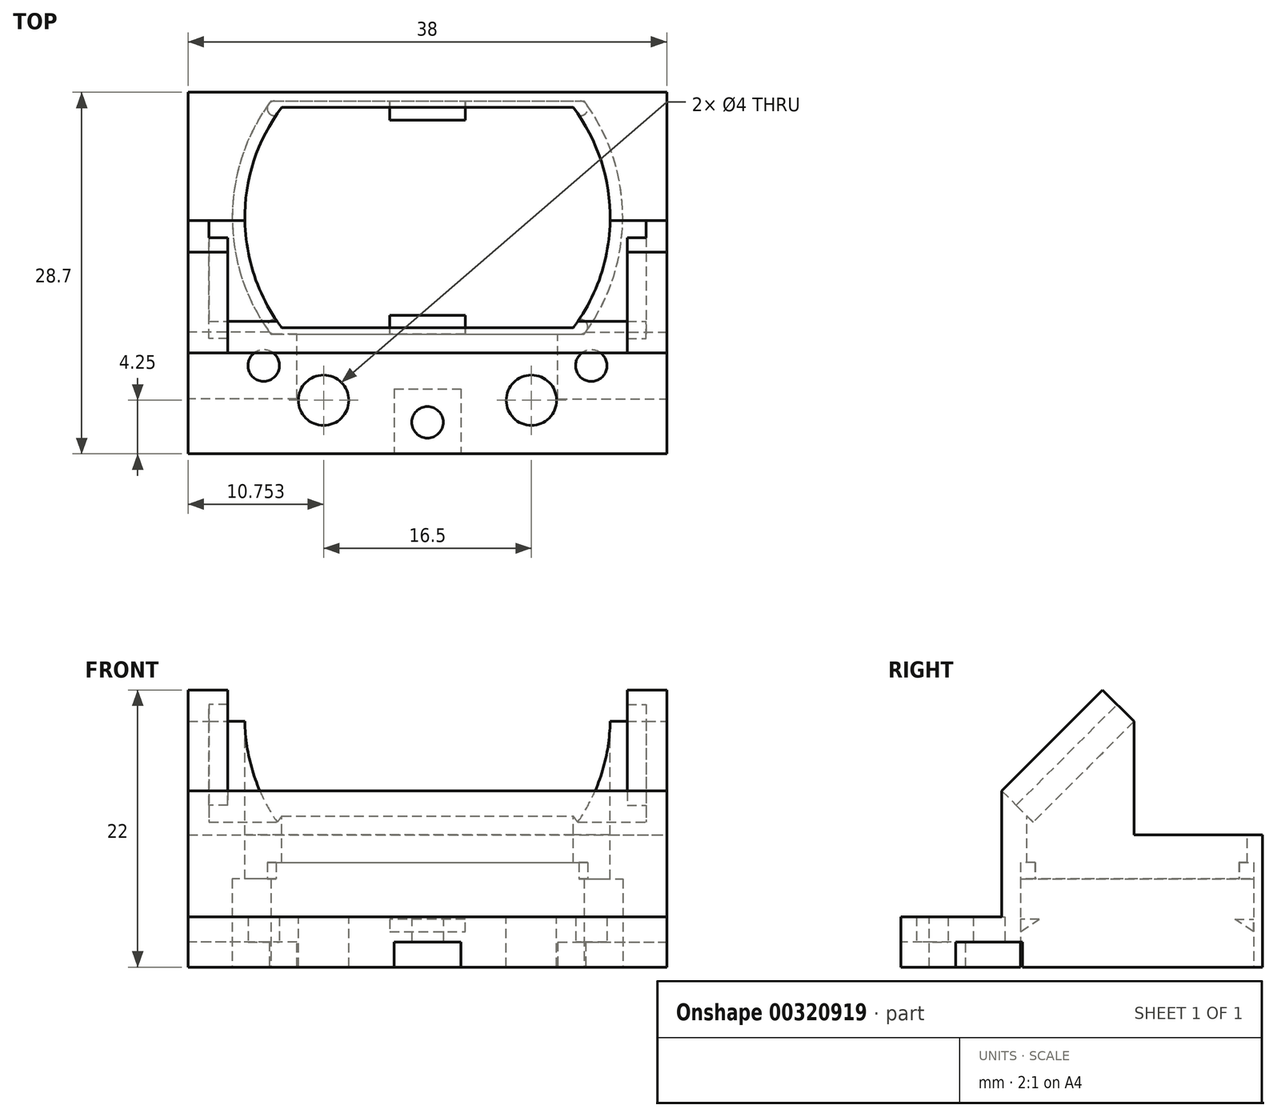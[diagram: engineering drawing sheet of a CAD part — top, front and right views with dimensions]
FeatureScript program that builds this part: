
annotation { "Feature Type Name" : "Feature", "Feature Type Description" : "" }
export const myFeature = defineFeature(function(context is Context, id is Id, definition is map)
    precondition{}
    {
        {
            var Q0;
            Q0=qCreatedBy(makeId("Top.planeOp"),FACE);
            var sketch = newSketch(context, id + "F0", { "sketchPlane" : qUnion([Q0])});
            skLineSegment(sketch, "E0.bottom", {"start": v(-15.89, 0) * mm, "end": v(22.11, 0) * mm});
            skLineSegment(sketch, "E0.top", {"start": v(-15.89, 28.5) * mm, "end": v(22.11, 28.5) * mm});
            skLineSegment(sketch, "E0.left", {"start": v(-15.89, 0) * mm, "end": v(-15.89, 28.5) * mm});
            skLineSegment(sketch, "E0.right", {"start": v(22.11, 0) * mm, "end": v(22.11, 28.5) * mm});
            skSolve(sketch);
        }
        {
            var Q0;
            Q0=qSketchRegion(id+"F0",true);
            extrude(context, id + "F1", {"entities" : qUnion([Q0]), "depth" : 19.5 * mm});
        }
        {
            var Q0;
            Q0=makeQuery(id+"F1.opExtrude","SWEPT_FACE",FACE,{"disambiguationData":[OSD([sQuery(id+"F0.wireOp",EDGE,"E0.right")])]});
            var sketch = newSketch(context, id + "F2", { "sketchPlane" : qUnion([Q0])});
            skLineSegment(sketch, "E1.bottom", {"start": v(0, 19.5) * mm, "end": v(8, 19.5) * mm});
            skLineSegment(sketch, "E1.top", {"start": v(0, 4) * mm, "end": v(8, 4) * mm});
            skLineSegment(sketch, "E1.left", {"start": v(0, 19.5) * mm, "end": v(0, 4) * mm});
            skLineSegment(sketch, "E1.right", {"start": v(8, 19.5) * mm, "end": v(8, 4) * mm});
            skSolve(sketch);
        }
        {
            var Q0;
            {var subQ4=sQuery(id+"F2.wireOp",EDGE,"E1.top");Q0=makeQuery(id+"F2.imprint","IMPRINT",FACE,{"disambiguationData":[TD([[makeQuery(id+"F2.imprint","IMPRINT",EDGE,{"derivedFrom":subQ4}),-1.0]])]});}
            var sketch = newSketch(context, id + "F3", { "sketchPlane" : qUnion([Q0])});
            skLineSegment(sketch, "E2.bottom", {"start": v(28.5, 19.5) * mm, "end": v(18.5, 19.5) * mm});
            skLineSegment(sketch, "E2.top", {"start": v(28.5, 10.5) * mm, "end": v(18.5, 10.5) * mm});
            skLineSegment(sketch, "E2.left", {"start": v(28.5, 19.5) * mm, "end": v(28.5, 10.5) * mm});
            skLineSegment(sketch, "E2.right", {"start": v(18.5, 19.5) * mm, "end": v(18.5, 10.5) * mm});
            skSolve(sketch);
        }
        {
            var Q0;
            Q0=makeQuery(id+"F2.imprint","IMPRINT",FACE,{"disambiguationData":[TD([[makeQuery(id+"F2.imprint","IMPRINT",EDGE,{"derivedFrom":sQuery(id+"F2.wireOp",EDGE,"E1.bottom")}),-1.0]])]});
            extrude(context, id + "F4", {"entities" : qUnion([Q0]), "operationType" : NewBodyOperationType.REMOVE, "oppositeDirection" : true, "depth" : 38 * mm});
        }
        {
            var Q0;
            Q0=makeQuery(id+"F1.opExtrude","CAP_FACE",FACE,{"disambiguationData":[OSD([sQuery(id+"F0.wireOp",EDGE,"E0.bottom"),sQuery(id+"F0.wireOp",EDGE,"E0.top"),sQuery(id+"F0.wireOp",EDGE,"E0.left"),sQuery(id+"F0.wireOp",EDGE,"E0.right")])],"isStart":false});
            var sketch = newSketch(context, id + "F5", { "sketchPlane" : qUnion([Q0])});
            skLineSegment(sketch, "E3.bottom", {"start": v(-8.45, 10) * mm, "end": v(14.68, 10) * mm});
            skLineSegment(sketch, "E3.top", {"start": v(-8.45, 27.5) * mm, "end": v(14.68, 27.5) * mm});
            skArc(sketch, "E4", {"start": v(14.68, 10) * mm, "mid": v(17.61, 18.75) * mm, "end": v(14.68, 27.5) * mm});
            skArc(sketch, "E5.trimOffspring", {"start": v(-8.45, 27.5) * mm, "mid": v(-11.39, 18.75) * mm, "end": v(-8.45, 10) * mm});
            skSolve(sketch);
        }
        {
            var Q0;
            Q0=qSketchRegion(id+"F5",true);
            extrude(context, id + "F6", {"entities" : qUnion([Q0]), "operationType" : NewBodyOperationType.REMOVE, "oppositeDirection" : true, "depth" : 19.5 * mm});
        }
        {
            var Q0;
            Q0=makeQuery(id+"F3.imprint","IMPRINT",FACE,{"disambiguationData":[TD([[makeQuery(id+"F3.imprint","IMPRINT",EDGE,{"derivedFrom":sQuery(id+"F3.wireOp",EDGE,"E2.bottom")}),-1.0]])]});
            extrude(context, id + "F7", {"entities" : qUnion([Q0]), "operationType" : NewBodyOperationType.REMOVE, "oppositeDirection" : true, "depth" : 38 * mm});
        }
        {
            var Q0;
            Q0=makeQuery(id+"F1.opExtrude","SWEPT_FACE",FACE,{"disambiguationData":[OSD([sQuery(id+"F0.wireOp",EDGE,"E0.right")])]});
            var sketch = newSketch(context, id + "F8", { "sketchPlane" : qUnion([Q0])});
            skLineSegment(sketch, "E6.bottom", {"start": v(8, 19.5) * mm, "end": v(18.5, 19.5) * mm});
            skLineSegment(sketch, "E6.left", {"start": v(8, 19.5) * mm, "end": v(8, 14) * mm});
            skLineSegment(sketch, "E7", {"start": v(18.5, 19.5) * mm, "end": v(10.5, 11.5) * mm});
            skLineSegment(sketch, "E8", {"start": v(8, 14) * mm, "end": v(10.5, 11.5) * mm});
            skSolve(sketch);
        }
        {
            var Q0;
            Q0=qSketchRegion(id+"F8",true);
            extrude(context, id + "F9", {"entities" : qUnion([Q0]), "operationType" : NewBodyOperationType.REMOVE, "oppositeDirection" : true, "depth" : 38 * mm});
        }
        {
            var Q0;
            Q0=makeQuery(id+"F1.opExtrude","CAP_FACE",FACE,{"disambiguationData":[OSD([sQuery(id+"F0.wireOp",EDGE,"E0.bottom"),sQuery(id+"F0.wireOp",EDGE,"E0.top"),sQuery(id+"F0.wireOp",EDGE,"E0.left"),sQuery(id+"F0.wireOp",EDGE,"E0.right")])],"isStart":true});
            var sketch = newSketch(context, id + "F10", { "sketchPlane" : qUnion([Q0])});
            skLineSegment(sketch, "E9.bottom", {"start": v(-9.32, -9.5) * mm, "end": v(15.55, -9.5) * mm});
            skLineSegment(sketch, "E9.top", {"start": v(-9.32, -28) * mm, "end": v(15.55, -28) * mm});
            skArc(sketch, "E10", {"start": v(-9.32, -9.5) * mm, "mid": v(-12.39, -18.75) * mm, "end": v(-9.32, -28) * mm});
            skArc(sketch, "E11.trimOffspring", {"start": v(15.55, -28) * mm, "mid": v(18.61, -18.75) * mm, "end": v(15.55, -9.5) * mm});
            skSolve(sketch);
        }
        {
            var Q0;
            Q0=qSketchRegion(id+"F10",true);
            extrude(context, id + "F11", {"entities" : qUnion([Q0]), "operationType" : NewBodyOperationType.REMOVE, "oppositeDirection" : true, "depth" : 7 * mm});
        }
        {
            var Q0;
            Q0=makeQuery(id+"F4.boolean.opBoolean","COPY",FACE,{"derivedFrom":makeQuery(id+"F4.opExtrude","SWEPT_FACE",FACE,{"disambiguationData":[OSD([sQuery(id+"F2.wireOp",EDGE,"E1.top")])]})});
            var sketch = newSketch(context, id + "F12", { "sketchPlane" : qUnion([Q0])});
            skCircle(sketch, "E12", {"center": v(-5.14, 4.25) * mm, "radius": 2 * mm});
            skCircle(sketch, "E13", {"center": v(11.36, 4.25) * mm, "radius": 2 * mm});
            skSolve(sketch);
        }
        {
            var Q0;
            Q0=makeQuery(id+"F12.imprint","IMPRINT",FACE,{"disambiguationData":[TD([[makeQuery(id+"F12.imprint","IMPRINT",EDGE,{"derivedFrom":sQuery(id+"F12.wireOp",EDGE,"E12")}),1.0]])]});
            var Q1;
            Q1=makeQuery(id+"F12.imprint","IMPRINT",FACE,{"disambiguationData":[TD([[makeQuery(id+"F12.imprint","IMPRINT",EDGE,{"derivedFrom":sQuery(id+"F12.wireOp",EDGE,"E13")}),1.0]])]});
            extrude(context, id + "F13", {"entities" : qUnion([Q0, Q1]), "operationType" : NewBodyOperationType.REMOVE, "oppositeDirection" : true, "depth" : 4 * mm});
        }
        {
            var Q0;
            Q0=makeQuery(id+"F1.opExtrude","SWEPT_FACE",FACE,{"disambiguationData":[OSD([sQuery(id+"F0.wireOp",EDGE,"E0.right")])]});
            var sketch = newSketch(context, id + "F14", { "sketchPlane" : qUnion([Q0])});
            skLineSegment(sketch, "E14", {"start": v(10.5, 11.5) * mm, "end": v(18.5, 19.5) * mm});
            skLineSegment(sketch, "E15", {"start": v(10.5, 11.5) * mm, "end": v(8, 14) * mm});
            skLineSegment(sketch, "E16", {"start": v(8, 14) * mm, "end": v(16, 22) * mm});
            skLineSegment(sketch, "E17", {"start": v(16, 22) * mm, "end": v(18.5, 19.5) * mm});
            skSolve(sketch);
        }
        {
            var Q0;
            Q0 = qSketchRegion(id + "F14", true);
            extrude(context, id + "F15", {"entities" : qUnion([Q0]), "operationType" : NewBodyOperationType.ADD, "oppositeDirection" : true, "depth" : 1.65 * mm, "offsetDistance" : 25 * mm});
        }
        {
            var Q0;
            Q0=makeQuery(id+"F15.opExtrude","CAP_FACE",FACE,{"disambiguationData":[OSD([sQuery(id+"F14.wireOp",EDGE,"E14"),sQuery(id+"F14.wireOp",EDGE,"E15"),sQuery(id+"F14.wireOp",EDGE,"E16"),sQuery(id+"F14.wireOp",EDGE,"E17")])],"isStart":false});
            var sketch = newSketch(context, id + "F16", { "sketchPlane" : qUnion([Q0])});
            skLineSegment(sketch, "E18", {"start": v(-8, 14) * mm, "end": v(-16, 22) * mm});
            skLineSegment(sketch, "E19", {"start": v(-16, 22) * mm, "end": v(-17.16, 20.84) * mm});
            skLineSegment(sketch, "E20", {"start": v(-17.16, 20.84) * mm, "end": v(-9.16, 12.84) * mm});
            skLineSegment(sketch, "E21", {"start": v(-9.16, 12.84) * mm, "end": v(-8, 14) * mm});
            skSolve(sketch);
        }
        {
            var Q0;
            Q0=makeQuery(id+"F16.imprint","IMPRINT",FACE,{"disambiguationData":[TD([[makeQuery(id+"F16.imprint","IMPRINT",EDGE,{"derivedFrom":sQuery(id+"F16.wireOp",EDGE,"E18")}),1.0]])]});
            extrude(context, id + "F17", {"entities" : qUnion([Q0]), "operationType" : NewBodyOperationType.ADD, "depth" : 1.5 * mm});
        }
        {
            var Q0;
            Q0=makeQuery(id+"F1.opExtrude","SWEPT_FACE",FACE,{"disambiguationData":[OSD([sQuery(id+"F0.wireOp",EDGE,"E0.left")])]});
            var sketch = newSketch(context, id + "F18", { "sketchPlane" : qUnion([Q0])});
            skLineSegment(sketch, "E22", {"start": v(-10.5, 11.5) * mm, "end": v(-8, 14) * mm});
            skLineSegment(sketch, "E23", {"start": v(-8, 14) * mm, "end": v(-16, 22) * mm});
            skLineSegment(sketch, "E24", {"start": v(-16, 22) * mm, "end": v(-18.5, 19.5) * mm});
            skLineSegment(sketch, "E25", {"start": v(-18.5, 19.5) * mm, "end": v(-10.5, 11.5) * mm});
            skSolve(sketch);
        }
        {
            var Q0;
            Q0=makeQuery(id+"F18.imprint","IMPRINT",FACE,{"disambiguationData":[TD([[makeQuery(id+"F18.imprint","IMPRINT",EDGE,{"derivedFrom":sQuery(id+"F18.wireOp",EDGE,"E22")}),-1.0]])]});
            extrude(context, id + "F19", {"entities" : qUnion([Q0]), "operationType" : NewBodyOperationType.ADD, "oppositeDirection" : true, "depth" : 1.65 * mm, "offsetDistance" : 25 * mm});
        }
        {
            var Q0;
            Q0=makeQuery(id+"F19.opExtrude","CAP_FACE",FACE,{"disambiguationData":[OSD([sQuery(id+"F18.wireOp",EDGE,"E22"),sQuery(id+"F18.wireOp",EDGE,"E23"),sQuery(id+"F18.wireOp",EDGE,"E24"),sQuery(id+"F18.wireOp",EDGE,"E25")])],"isStart":false});
            var sketch = newSketch(context, id + "F20", { "sketchPlane" : qUnion([Q0])});
            skLineSegment(sketch, "E26", {"start": v(16, 22) * mm, "end": v(8, 14) * mm});
            skLineSegment(sketch, "E27", {"start": v(8, 14) * mm, "end": v(9.16, 12.84) * mm});
            skLineSegment(sketch, "E28", {"start": v(9.16, 12.84) * mm, "end": v(17.16, 20.84) * mm});
            skLineSegment(sketch, "E29", {"start": v(17.16, 20.84) * mm, "end": v(16, 22) * mm});
            skSolve(sketch);
        }
        {
            var Q0;
            Q0 = qSketchRegion(id + "F20", true);
            extrude(context, id + "F21", {"entities" : qUnion([Q0]), "operationType" : NewBodyOperationType.ADD, "depth" : 1.5 * mm});
        }
        {
            var Q0;
            Q0=makeQuery(id+"F11.boolean.opBoolean","COPY",FACE,{"derivedFrom":makeQuery(id+"F11.opExtrude","SWEPT_FACE",FACE,{"disambiguationData":[OSD([sQuery(id+"F10.wireOp",EDGE,"E9.bottom")])]})});
            var sketch = newSketch(context, id + "F22", { "sketchPlane" : qUnion([Q0])});
            skLineSegment(sketch, "E30", {"start": v(-3.11, 3.8) * mm, "end": v(-0.11, 3.8) * mm});
            skPoint(sketch, "E30.startSnap0", {"position": v(-3.11, 7) * mm});
            skLineSegment(sketch, "E31", {"start": v(-0.11, 3.8) * mm, "end": v(-0.11, 2.8) * mm});
            skLineSegment(sketch, "E32", {"start": v(-0.11, 2.8) * mm, "end": v(-6.11, 2.8) * mm});
            skLineSegment(sketch, "E33", {"start": v(-6.11, 2.8) * mm, "end": v(-6.11, 3.8) * mm});
            skLineSegment(sketch, "E34", {"start": v(-6.11, 3.8) * mm, "end": v(-3.11, 3.8) * mm});
            skSolve(sketch);
        }
        {
            var Q0;
            Q0 = qSketchRegion(id + "F22", true);
            extrude(context, id + "F23", {"entities" : qUnion([Q0]), "operationType" : NewBodyOperationType.ADD, "depth" : 1.5 * mm});
        }
        {
            var Q0;
            Q0=makeQuery(id+"F23.opExtrude","SWEPT_FACE",FACE,{"disambiguationData":[OSD([sQuery(id+"F22.wireOp",EDGE,"E31")])]});
            var sketch = newSketch(context, id + "F24", { "sketchPlane" : qUnion([Q0])});
            skLineSegment(sketch, "E35", {"start": v(-9.5, 2.8) * mm, "end": v(-11, 3.8) * mm});
            skLineSegment(sketch, "E36", {"start": v(-11, 3.8) * mm, "end": v(-11, 2.8) * mm});
            skLineSegment(sketch, "E37", {"start": v(-11, 2.8) * mm, "end": v(-9.5, 2.8) * mm});
            skSolve(sketch);
        }
        {
            var Q0;
            Q0 = qSketchRegion(id + "F24", true);
            extrude(context, id + "F25", {"entities" : qUnion([Q0]), "operationType" : NewBodyOperationType.REMOVE, "oppositeDirection" : true, "depth" : 6 * mm});
        }
        {
            var Q0;
            Q0=makeQuery(id+"F11.boolean.opBoolean","COPY",FACE,{"derivedFrom":makeQuery(id+"F11.opExtrude","SWEPT_FACE",FACE,{"disambiguationData":[OSD([sQuery(id+"F10.wireOp",EDGE,"E9.top")])]})});
            var sketch = newSketch(context, id + "F26", { "sketchPlane" : qUnion([Q0])});
            skLineSegment(sketch, "E38", {"start": v(3.11, 3.8) * mm, "end": v(6.11, 3.8) * mm});
            skPoint(sketch, "E38.startSnap0", {"position": v(3.11, 7) * mm});
            skLineSegment(sketch, "E39", {"start": v(6.11, 3.8) * mm, "end": v(6.11, 2.8) * mm});
            skLineSegment(sketch, "E40", {"start": v(6.11, 2.8) * mm, "end": v(0.11, 2.8) * mm});
            skLineSegment(sketch, "E41", {"start": v(0.11, 2.8) * mm, "end": v(0.11, 3.8) * mm});
            skLineSegment(sketch, "E42", {"start": v(0.11, 3.8) * mm, "end": v(3.11, 3.8) * mm});
            skSolve(sketch);
        }
        {
            var Q0;
            Q0 = qSketchRegion(id + "F26", true);
            extrude(context, id + "F27", {"entities" : qUnion([Q0]), "operationType" : NewBodyOperationType.ADD, "depth" : 1.5 * mm});
        }
        {
            var Q0;
            Q0=makeQuery(id+"F27.opExtrude","SWEPT_FACE",FACE,{"disambiguationData":[OSD([sQuery(id+"F26.wireOp",EDGE,"E41")])]});
            var sketch = newSketch(context, id + "F28", { "sketchPlane" : qUnion([Q0])});
            skLineSegment(sketch, "E43", {"start": v(-28, 2.8) * mm, "end": v(-26.5, 3.8) * mm});
            skLineSegment(sketch, "E44", {"start": v(-26.5, 3.8) * mm, "end": v(-26.5, 2.8) * mm});
            skLineSegment(sketch, "E45", {"start": v(-26.5, 2.8) * mm, "end": v(-28, 2.8) * mm});
            skSolve(sketch);
        }
        {
            var Q0;
            Q0 = qSketchRegion(id + "F28", true);
            extrude(context, id + "F29", {"entities" : qUnion([Q0]), "operationType" : NewBodyOperationType.REMOVE, "oppositeDirection" : true, "depth" : 6 * mm});
        }
        {
            var Q0;
            Q0=makeQuery(id+"F1.opExtrude","SWEPT_FACE",FACE,{"disambiguationData":[OSD([sQuery(id+"F0.wireOp",EDGE,"E0.top")])]});
            var sketch = newSketch(context, id + "F30", { "sketchPlane" : qUnion([Q0])});
            skLineSegment(sketch, "E46.bottom", {"start": v(15.89, 0) * mm, "end": v(-22.11, 0) * mm});
            skLineSegment(sketch, "E46.top", {"start": v(15.89, 10.5) * mm, "end": v(-22.11, 10.5) * mm});
            skLineSegment(sketch, "E46.left", {"start": v(15.89, 0) * mm, "end": v(15.89, 10.5) * mm});
            skLineSegment(sketch, "E46.right", {"start": v(-22.11, 0) * mm, "end": v(-22.11, 10.5) * mm});
            skSolve(sketch);
        }
        {
            var Q0;
            Q0 = qSketchRegion(id + "F30", true);
            extrude(context, id + "F31", {"entities" : qUnion([Q0]), "operationType" : NewBodyOperationType.ADD, "depth" : 0.2 * mm});
        }
        {
            var Q0;
            Q0=makeQuery(id+"F11.boolean.opBoolean","COPY",FACE,{"derivedFrom":makeQuery(id+"F11.opExtrude","CAP_FACE",FACE,{"disambiguationData":[OSD([sQuery(id+"F10.wireOp",EDGE,"E9.bottom"),sQuery(id+"F10.wireOp",EDGE,"E9.top"),sQuery(id+"F10.wireOp",EDGE,"E10"),sQuery(id+"F10.wireOp",EDGE,"E11.trimOffspring")])],"isStart":false})});
            var sketch = newSketch(context, id + "F32", { "sketchPlane" : qUnion([Q0])});
            skLineSegment(sketch, "E47", {"start": v(-8.45, -10.08) * mm, "end": v(-8.45, -27.42) * mm});
            skLineSegment(sketch, "E48", {"start": v(-9.03, -28) * mm, "end": v(15.26, -28) * mm});
            skLineSegment(sketch, "E49", {"start": v(14.68, -27.42) * mm, "end": v(14.68, -10.08) * mm});
            skLineSegment(sketch, "E50", {"start": v(15.26, -9.5) * mm, "end": v(-9.03, -9.5) * mm});
            skArc(sketch, "E51", {"start": v(-8.45, -27.42) * mm, "mid": v(-9.44, -27) * mm, "end": v(-9.03, -28) * mm});
            skArc(sketch, "E52", {"start": v(-9.03, -9.5) * mm, "mid": v(-9.44, -10.5) * mm, "end": v(-8.45, -10.08) * mm});
            skPoint(sketch, "E53.orphan", {"position": v(-8.45, -9.5) * mm});
            skArc(sketch, "E54", {"start": v(15.26, -28) * mm, "mid": v(15.67, -27) * mm, "end": v(14.68, -27.42) * mm});
            skPoint(sketch, "E55.orphan", {"position": v(14.68, -28) * mm});
            skArc(sketch, "E56", {"start": v(14.68, -10.08) * mm, "mid": v(15.67, -10.5) * mm, "end": v(15.26, -9.5) * mm});
            skSolve(sketch);
        }
        {
            var Q0;
            Q0 = qSketchRegion(id + "F32", true);
            extrude(context, id + "F33", {"entities" : qUnion([Q0]), "operationType" : NewBodyOperationType.REMOVE, "oppositeDirection" : true, "depth" : 1.3 * mm});
        }
        {
            var Q0;
            Q0=makeQuery(id+"F31.boolean.opBoolean","MERGE",FACE,{"derivedFrom":[makeQuery(id+"F1.opExtrude","CAP_FACE",FACE,{"disambiguationData":[OSD([sQuery(id+"F0.wireOp",EDGE,"E0.bottom"),sQuery(id+"F0.wireOp",EDGE,"E0.top"),sQuery(id+"F0.wireOp",EDGE,"E0.left"),sQuery(id+"F0.wireOp",EDGE,"E0.right")])],"isStart":true}),makeQuery(id+"F31.opExtrude","SWEPT_FACE",FACE,{"disambiguationData":[OSD([sQuery(id+"F30.wireOp",EDGE,"E46.bottom")])]})]});
            var sketch = newSketch(context, id + "F34", { "sketchPlane" : qUnion([Q0])});
            skCircle(sketch, "E57", {"center": v(-9.89, -7) * mm, "radius": 1.25 * mm});
            skCircle(sketch, "E58", {"center": v(16.11, -7) * mm, "radius": 1.25 * mm});
            skCircle(sketch, "E59", {"center": v(3.11, -2.5) * mm, "radius": 1.25 * mm});
            skSolve(sketch);
        }
        {
            var Q0;
            Q0 = qSketchRegion(id + "F34", true);
            extrude(context, id + "F35", {"entities" : qUnion([Q0]), "operationType" : NewBodyOperationType.REMOVE, "oppositeDirection" : true, "depth" : 4 * mm, "offsetDistance" : 25 * mm});
        }
        {
            var Q0;
            Q0=makeQuery(id+"F31.boolean.opBoolean","MERGE",FACE,{"derivedFrom":[makeQuery(id+"F19.boolean.opBoolean","MERGE",FACE,{"derivedFrom":[makeQuery(id+"F1.opExtrude","SWEPT_FACE",FACE,{"disambiguationData":[OSD([sQuery(id+"F0.wireOp",EDGE,"E0.left")])]}),makeQuery(id+"F19.opExtrude","CAP_FACE",FACE,{"disambiguationData":[OSD([sQuery(id+"F18.wireOp",EDGE,"E22"),sQuery(id+"F18.wireOp",EDGE,"E23"),sQuery(id+"F18.wireOp",EDGE,"E24"),sQuery(id+"F18.wireOp",EDGE,"E25")])],"isStart":true})]}),makeQuery(id+"F31.opExtrude","SWEPT_FACE",FACE,{"disambiguationData":[OSD([sQuery(id+"F30.wireOp",EDGE,"E46.left")])]})]});
            var sketch = newSketch(context, id + "F36", { "sketchPlane" : qUnion([Q0])});
            skLineSegment(sketch, "E60", {"start": v(-9.65, 0) * mm, "end": v(-9.65, 2) * mm});
            skLineSegment(sketch, "E61", {"start": v(-9.65, 2) * mm, "end": v(-4.35, 2) * mm});
            skLineSegment(sketch, "E62", {"start": v(-4.35, 2) * mm, "end": v(-4.35, 0) * mm});
            skLineSegment(sketch, "E63", {"start": v(-4.35, 0) * mm, "end": v(-9.65, 0) * mm});
            skPoint(sketch, "E64", {"position": v(-7, 0) * mm});
            skSolve(sketch);
        }
        {
            var Q0;
            Q0 = qSketchRegion(id + "F36", true);
            extrude(context, id + "F37", {"entities" : qUnion([Q0]), "operationType" : NewBodyOperationType.REMOVE, "oppositeDirection" : true, "depth" : 8.65 * mm, "offsetDistance" : 25 * mm});
        }
        {
            var Q0;
            Q0=makeQuery(id+"F31.boolean.opBoolean","MERGE",FACE,{"derivedFrom":[makeQuery(id+"F15.boolean.opBoolean","MERGE",FACE,{"derivedFrom":[makeQuery(id+"F1.opExtrude","SWEPT_FACE",FACE,{"disambiguationData":[OSD([sQuery(id+"F0.wireOp",EDGE,"E0.right")])]}),makeQuery(id+"F15.opExtrude","CAP_FACE",FACE,{"disambiguationData":[OSD([sQuery(id+"F14.wireOp",EDGE,"E14"),sQuery(id+"F14.wireOp",EDGE,"E15"),sQuery(id+"F14.wireOp",EDGE,"E16"),sQuery(id+"F14.wireOp",EDGE,"E17")])],"isStart":true})]}),makeQuery(id+"F31.opExtrude","SWEPT_FACE",FACE,{"disambiguationData":[OSD([sQuery(id+"F30.wireOp",EDGE,"E46.right")])]})]});
            var sketch = newSketch(context, id + "F38", { "sketchPlane" : qUnion([Q0])});
            skLineSegment(sketch, "E65", {"start": v(9.65, 0) * mm, "end": v(9.65, 2) * mm});
            skLineSegment(sketch, "E66", {"start": v(9.65, 2) * mm, "end": v(4.35, 2) * mm});
            skLineSegment(sketch, "E67", {"start": v(4.35, 2) * mm, "end": v(4.35, 0) * mm});
            skLineSegment(sketch, "E68", {"start": v(4.35, 0) * mm, "end": v(9.65, 0) * mm});
            skPoint(sketch, "E69", {"position": v(7, 0) * mm});
            skSolve(sketch);
        }
        {
            var Q0;
            Q0 = qSketchRegion(id + "F38", true);
            extrude(context, id + "F39", {"entities" : qUnion([Q0]), "operationType" : NewBodyOperationType.REMOVE, "oppositeDirection" : true, "depth" : 8.65 * mm, "offsetDistance" : 25 * mm});
        }
        {
            var Q0;
            Q0=makeQuery(id+"F1.opExtrude","SWEPT_FACE",FACE,{"disambiguationData":[OSD([sQuery(id+"F0.wireOp",EDGE,"E0.bottom")])]});
            var sketch = newSketch(context, id + "F40", { "sketchPlane" : qUnion([Q0])});
            skLineSegment(sketch, "E70", {"start": v(5.76, 0) * mm, "end": v(5.76, 2) * mm});
            skLineSegment(sketch, "E71", {"start": v(5.76, 2) * mm, "end": v(0.46, 2) * mm});
            skLineSegment(sketch, "E72", {"start": v(0.46, 2) * mm, "end": v(0.46, 0) * mm});
            skLineSegment(sketch, "E73", {"start": v(0.46, 0) * mm, "end": v(5.76, 0) * mm});
            skPoint(sketch, "E74", {"position": v(3.11, 0) * mm});
            skSolve(sketch);
        }
        {
            var Q0;
            Q0 = qSketchRegion(id + "F40", true);
            extrude(context, id + "F41", {"entities" : qUnion([Q0]), "operationType" : NewBodyOperationType.REMOVE, "oppositeDirection" : true, "depth" : 5.15 * mm, "offsetDistance" : 25 * mm});
        }
    });
